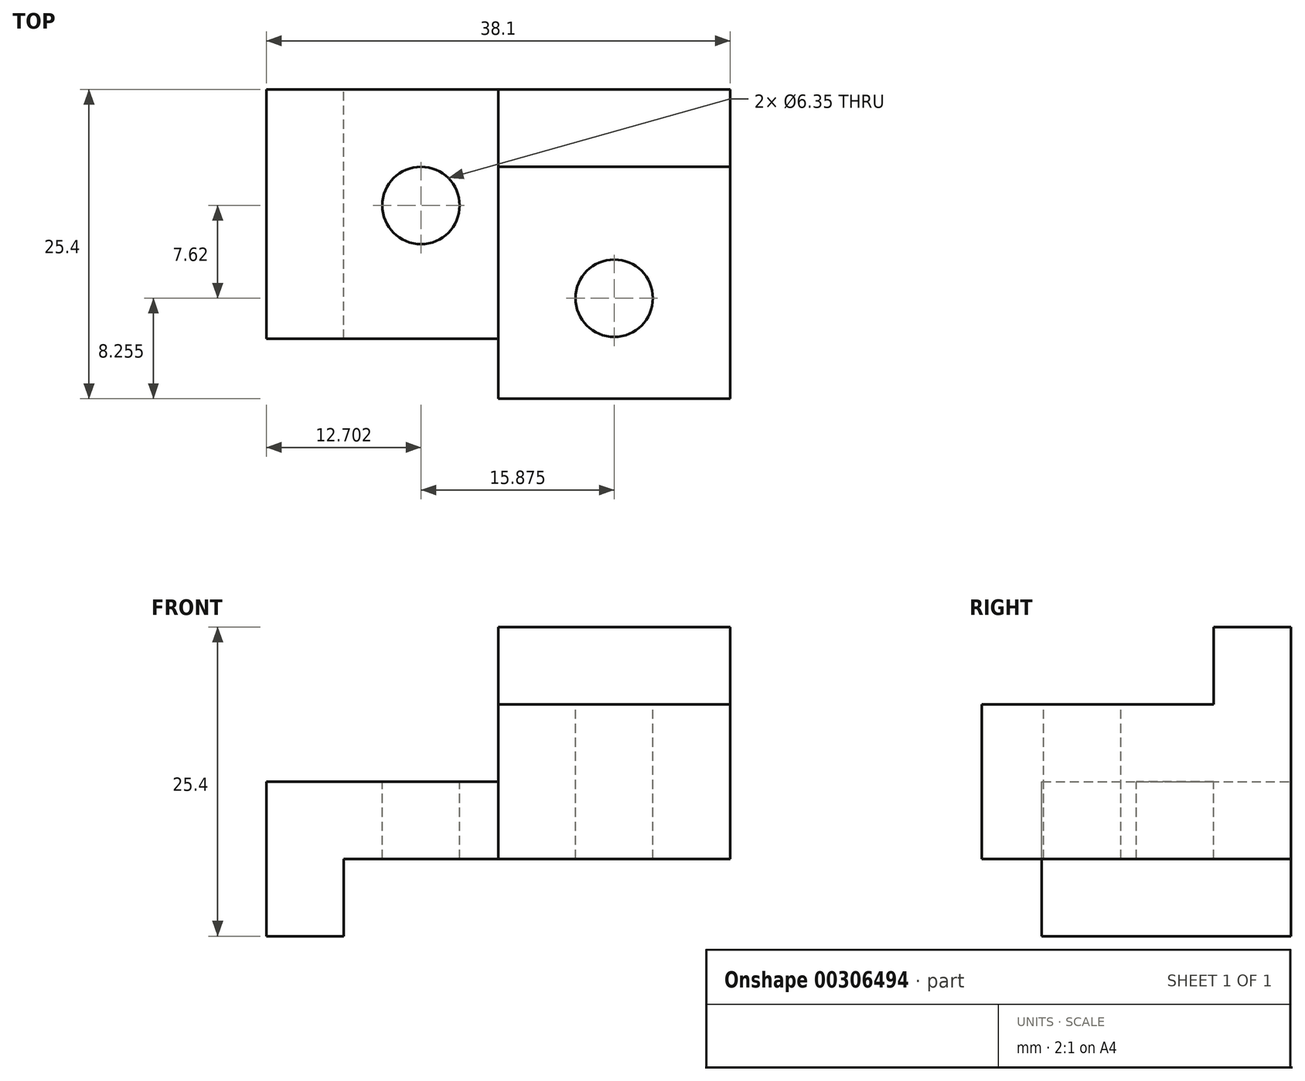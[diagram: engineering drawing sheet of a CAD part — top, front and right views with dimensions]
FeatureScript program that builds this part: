
annotation { "Feature Type Name" : "Feature", "Feature Type Description" : "" }
export const myFeature = defineFeature(function(context is Context, id is Id, definition is map)
    precondition{}
    {
        {
            var Q0;
            Q0=qCreatedBy(makeId("Front.planeOp"),FACE);
            var sketch = newSketch(context, id + "F0", { "sketchPlane" : qUnion([Q0])});
            skLineSegment(sketch, "E0", {"start": v(-24.83, 0) * mm, "end": v(-18.48, 0) * mm});
            skLineSegment(sketch, "E1", {"start": v(-18.48, 0) * mm, "end": v(-18.48, 6.35) * mm});
            skLineSegment(sketch, "E2", {"start": v(-24.83, 12.7) * mm, "end": v(-24.83, 0) * mm});
            skLineSegment(sketch, "E3", {"start": v(-5.78, 25.4) * mm, "end": v(13.27, 25.4) * mm});
            skLineSegment(sketch, "E4", {"start": v(13.27, 25.4) * mm, "end": v(13.27, 6.35) * mm});
            skLineSegment(sketch, "E5", {"start": v(-18.48, 6.35) * mm, "end": v(13.27, 6.35) * mm});
            skLineSegment(sketch, "E6", {"start": v(-5.78, 25.4) * mm, "end": v(-5.78, 12.7) * mm});
            skLineSegment(sketch, "E7", {"start": v(-5.78, 12.7) * mm, "end": v(-24.83, 12.7) * mm});
            skSolve(sketch);
        }
        {
            var Q0;
            Q0 = qSketchRegion(id + "F0", true);
            extrude(context, id + "F1", {"entities" : qUnion([Q0]), "depth" : 25.4 * mm});
        }
        {
            var Q0;
            Q0=makeQuery(id+"F1.opExtrude","SWEPT_FACE",FACE,{"disambiguationData":[OSD([sQuery(id+"F0.wireOp",EDGE,"E7")])]});
            var sketch = newSketch(context, id + "F2", { "sketchPlane" : qUnion([Q0])});
            skLineSegment(sketch, "E8", {"start": v(-24.83, -20.48) * mm, "end": v(-5.78, -20.48) * mm});
            skLineSegment(sketch, "E9", {"start": v(-5.78, -20.48) * mm, "end": v(-5.78, -25.4) * mm});
            skLineSegment(sketch, "E10", {"start": v(-5.78, -25.4) * mm, "end": v(-24.83, -25.4) * mm});
            skLineSegment(sketch, "E11", {"start": v(-24.83, -25.4) * mm, "end": v(-24.83, -20.48) * mm});
            skSolve(sketch);
        }
        {
            var Q0;
            Q0=makeQuery(id+"F2.imprint","IMPRINT",FACE,{"disambiguationData":[TD([[makeQuery(id+"F2.imprint","IMPRINT",EDGE,{"derivedFrom":sQuery(id+"F2.wireOp",EDGE,"E8")}),-1.0]])]});
            extrude(context, id + "F3", {"entities" : qUnion([Q0]), "operationType" : NewBodyOperationType.REMOVE, "oppositeDirection" : true, "depth" : 25.4 * mm});
        }
        {
            var Q0;
            Q0=makeQuery(id+"F1.opExtrude","SWEPT_FACE",FACE,{"disambiguationData":[OSD([sQuery(id+"F0.wireOp",EDGE,"E7")])]});
            var sketch = newSketch(context, id + "F4", { "sketchPlane" : qUnion([Q0])});
            skCircle(sketch, "E12", {"center": v(-12.13, -9.53) * mm, "radius": 3.18 * mm});
            skSolve(sketch);
        }
        {
            var Q0;
            Q0 = qSketchRegion(id + "F4", true);
            extrude(context, id + "F5", {"entities" : qUnion([Q0]), "operationType" : NewBodyOperationType.REMOVE, "endBound" : BoundingType.THROUGH_ALL, "oppositeDirection" : true, "depth" : 25.4 * mm});
        }
        {
            var Q0;
            Q0=makeQuery(id+"F1.opExtrude","SWEPT_FACE",FACE,{"disambiguationData":[OSD([sQuery(id+"F0.wireOp",EDGE,"E3")])]});
            var sketch = newSketch(context, id + "F6", { "sketchPlane" : qUnion([Q0])});
            skCircle(sketch, "E13", {"center": v(3.75, -17.15) * mm, "radius": 3.18 * mm});
            skSolve(sketch);
        }
        {
            var Q0;
            Q0 = qSketchRegion(id + "F6", true);
            extrude(context, id + "F7", {"entities" : qUnion([Q0]), "operationType" : NewBodyOperationType.REMOVE, "oppositeDirection" : true, "depth" : 25.4 * mm});
        }
        {
            var Q0;
            Q0=makeQuery(id+"F1.opExtrude","SWEPT_FACE",FACE,{"disambiguationData":[OSD([sQuery(id+"F0.wireOp",EDGE,"E3")])]});
            var sketch = newSketch(context, id + "F8", { "sketchPlane" : qUnion([Q0])});
            skLineSegment(sketch, "E14", {"start": v(-5.78, -6.35) * mm, "end": v(13.27, -6.35) * mm});
            skLineSegment(sketch, "E15", {"start": v(13.27, -6.35) * mm, "end": v(13.27, -25.4) * mm});
            skLineSegment(sketch, "E16", {"start": v(13.27, -25.4) * mm, "end": v(-5.78, -25.4) * mm});
            skLineSegment(sketch, "E17", {"start": v(-5.78, -25.4) * mm, "end": v(-5.78, -6.35) * mm});
            skSolve(sketch);
        }
        {
            var Q0;
            Q0 = qSketchRegion(id + "F8", true);
            extrude(context, id + "F9", {"entities" : qUnion([Q0]), "operationType" : NewBodyOperationType.REMOVE, "oppositeDirection" : true, "depth" : 6.35 * mm});
        }
    });
